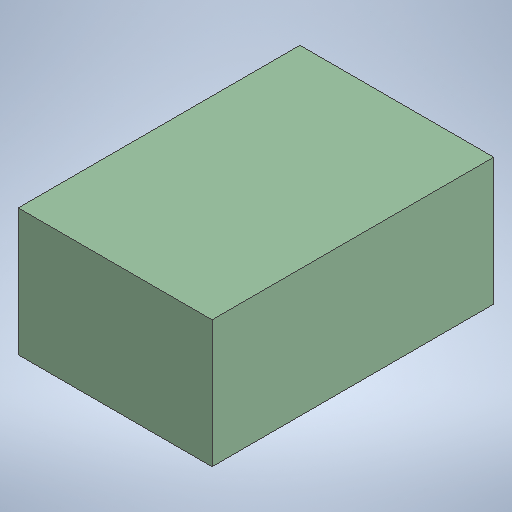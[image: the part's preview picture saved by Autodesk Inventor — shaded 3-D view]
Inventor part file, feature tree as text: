
AUTODESK INVENTOR PART (.ipt)
format: ipt  version: 2025.1 (Build 291241000, 241)  size: 176,640 bytes
history: native  units: in
note: dims shown in document units (in); Inventor stores cm internally (conversion verified against a paired STEP export)
features: extrude x1, sketch x1, other x1
ambient origin geometry x8: Origin, YZ Plane, XZ Plane, XY Plane, X Axis, Y Axis, Z Axis, Center Point
bodies: Solid1 (feature_tree)
feature tree (3):
  extrude  "Extrusion1"  Depth=3.6614in
  sketch  "Sketch1"  dims[d0=2.5197in d1=3.6614in d2=1.6535in d3=0.0in]
  other  "Finish1"
